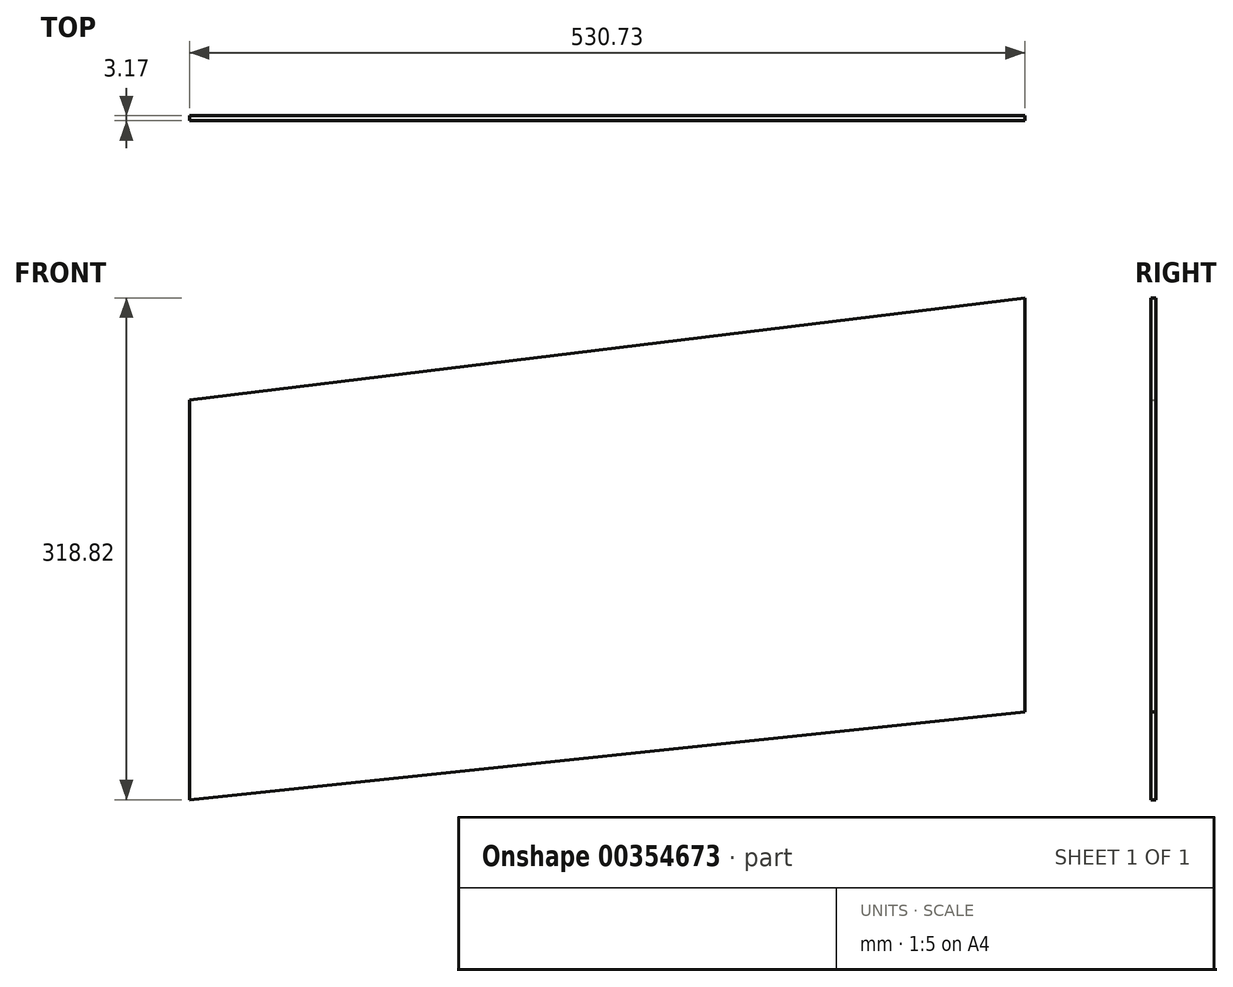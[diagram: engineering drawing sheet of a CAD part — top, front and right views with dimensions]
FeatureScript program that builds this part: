
annotation { "Feature Type Name" : "Feature", "Feature Type Description" : "" }
export const myFeature = defineFeature(function(context is Context, id is Id, definition is map)
    precondition{}
    {
        {
            var Q0;
            Q0=qCreatedBy(makeId("Front.planeOp"),FACE);
            var sketch = newSketch(context, id + "F0", { "sketchPlane" : qUnion([Q0])});
            skLineSegment(sketch, "E0", {"start": v(-268.64, 135.96) * mm, "end": v(-268.64, -118.04) * mm});
            skLineSegment(sketch, "E1", {"start": v(-268.64, -118.04) * mm, "end": v(261.84, -62.29) * mm});
            skLineSegment(sketch, "E2", {"start": v(261.84, -62.29) * mm, "end": v(262.09, 200.78) * mm});
            skLineSegment(sketch, "E3", {"start": v(262.09, 200.78) * mm, "end": v(-268.64, 135.96) * mm});
            skSolve(sketch);
        }
        {
            var Q0;
            Q0=qSketchRegion(id+"F0",true);
            extrude(context, id + "F1", {"entities" : qUnion([Q0]), "depth" : 3.17 * mm});
        }
    });
